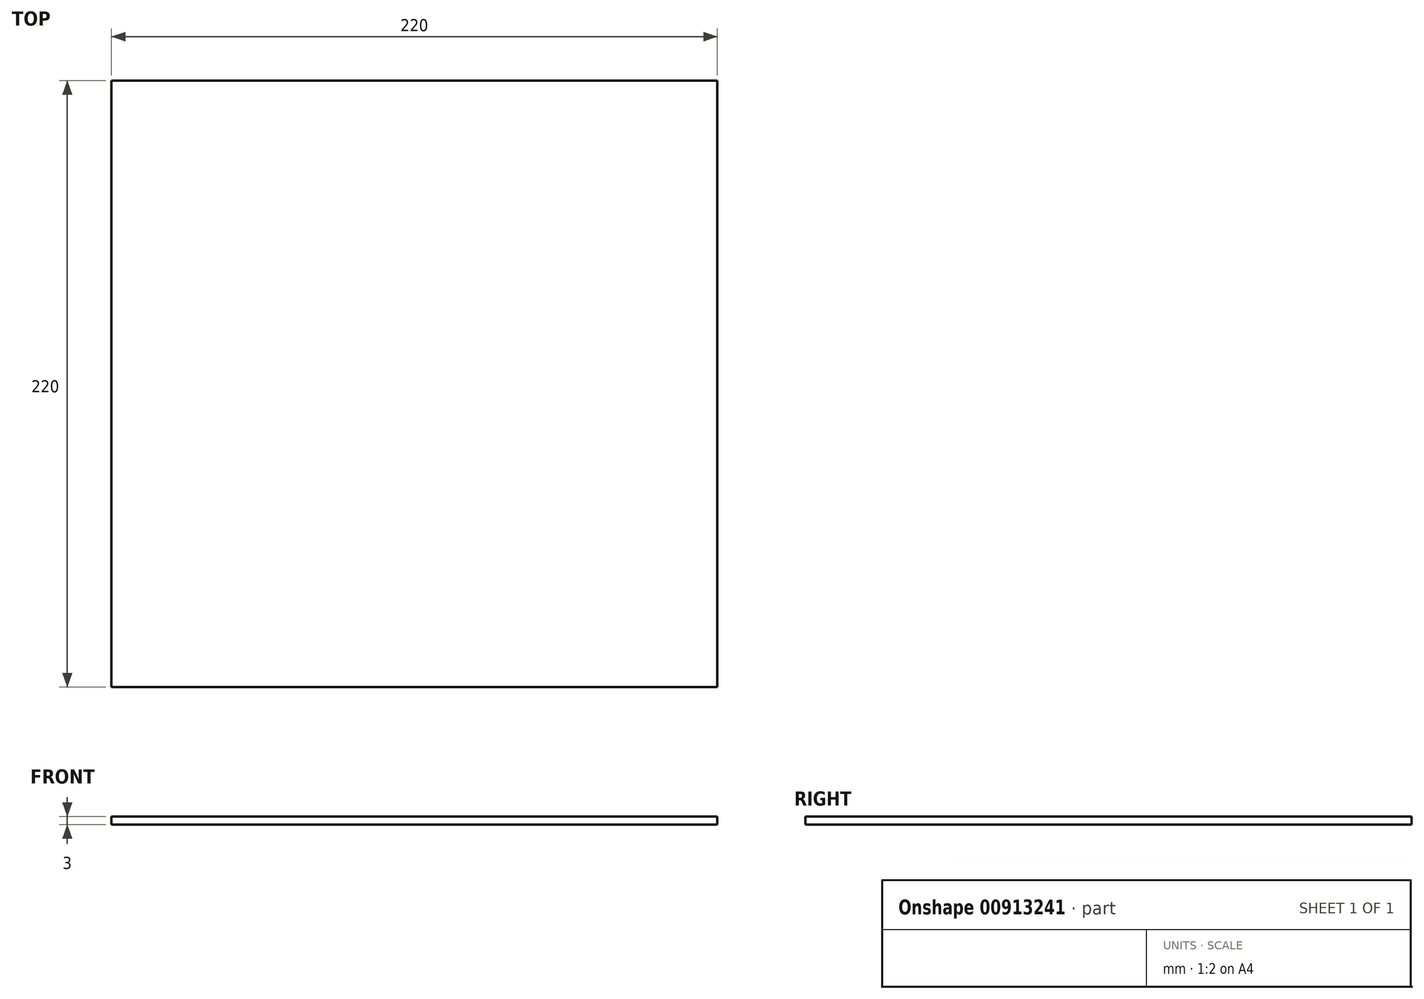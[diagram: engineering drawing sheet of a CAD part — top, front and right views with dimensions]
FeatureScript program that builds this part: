
annotation { "Feature Type Name" : "Feature", "Feature Type Description" : "" }
export const myFeature = defineFeature(function(context is Context, id is Id, definition is map)
    precondition{}
    {
        {
            var Q0;
            Q0=qCreatedBy(makeId("Top.planeOp"),FACE);
            var sketch = newSketch(context, id + "F0", { "sketchPlane" : qUnion([Q0])});
            skLineSegment(sketch, "E0.bottom", {"start": v(110, -110) * mm, "end": v(-110, -110) * mm});
            skLineSegment(sketch, "E0.top", {"start": v(110, 110) * mm, "end": v(-110, 110) * mm});
            skLineSegment(sketch, "E0.left", {"start": v(110, -110) * mm, "end": v(110, 110) * mm});
            skLineSegment(sketch, "E0.right", {"start": v(-110, -110) * mm, "end": v(-110, 110) * mm});
            skPoint(sketch, "E0.middle", {"position": v(0, 0) * mm});
            skSolve(sketch);
        }
        {
            var Q0;
            Q0=makeQuery(id+"F0.imprint","IMPRINT",FACE,{"disambiguationData":[TD([[makeQuery(id+"F0.imprint","IMPRINT",EDGE,{"derivedFrom":sQuery(id+"F0.wireOp",EDGE,"E0.bottom")}),-1.0]])]});
            extrude(context, id + "F1", {"entities" : qUnion([Q0]), "depth" : 3 * mm, "offsetDistance" : 25 * mm});
        }
    });
